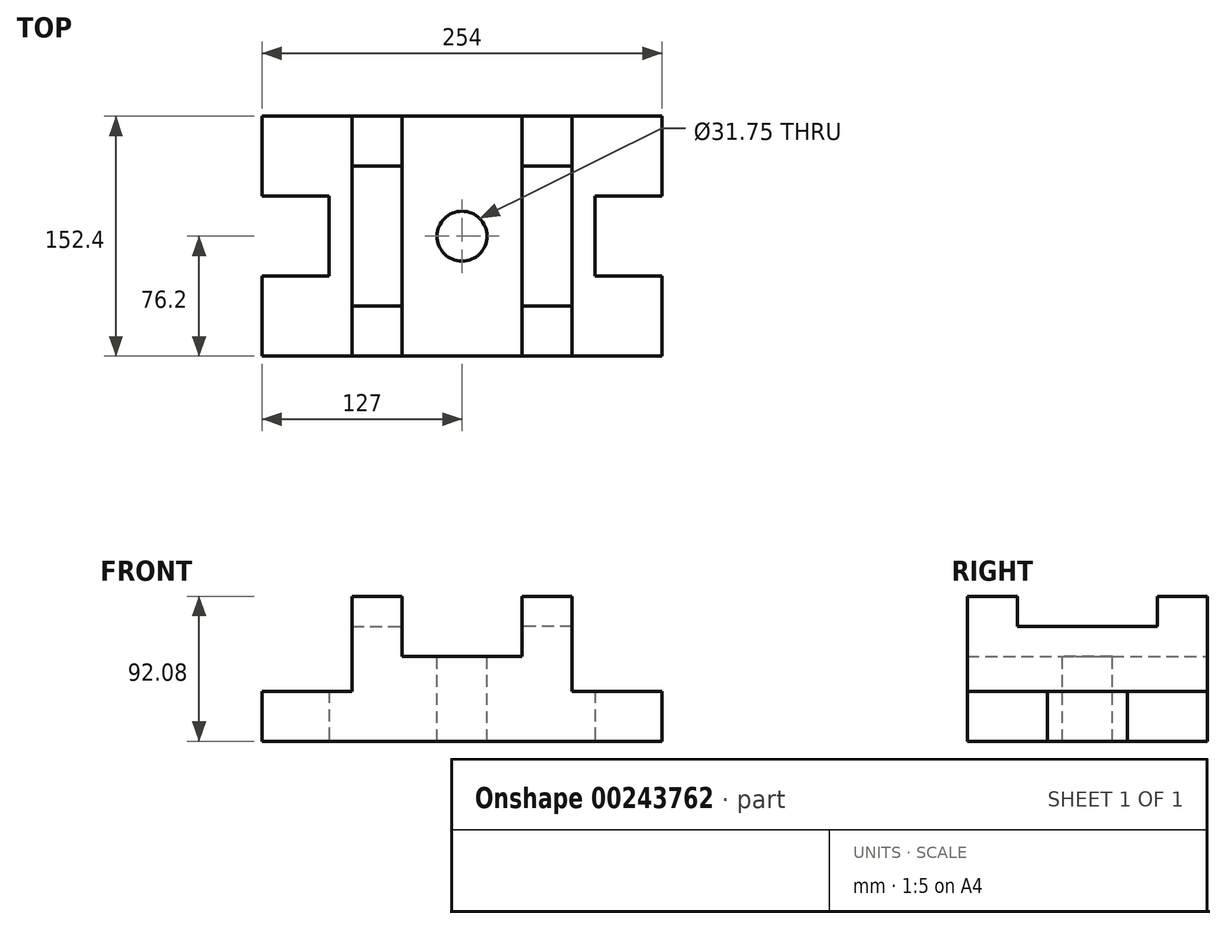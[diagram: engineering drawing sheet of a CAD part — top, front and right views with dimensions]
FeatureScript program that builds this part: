
annotation { "Feature Type Name" : "Feature", "Feature Type Description" : "" }
export const myFeature = defineFeature(function(context is Context, id is Id, definition is map)
    precondition{}
    {
        {
            var Q0;
            Q0=qCreatedBy(makeId("Front.planeOp"),FACE);
            var sketch = newSketch(context, id + "F0", { "sketchPlane" : qUnion([Q0])});
            skLineSegment(sketch, "E0", {"start": v(0, 0) * mm, "end": v(-63.5, 0) * mm});
            skLineSegment(sketch, "E1", {"start": v(0, 0) * mm, "end": v(63.5, 0) * mm});
            skLineSegment(sketch, "E2", {"start": v(63.5, 0) * mm, "end": v(63.5, 31.75) * mm});
            skLineSegment(sketch, "E3", {"start": v(63.5, 31.75) * mm, "end": v(6.35, 31.75) * mm});
            skLineSegment(sketch, "E4", {"start": v(6.35, 31.75) * mm, "end": v(6.35, 92.07) * mm});
            skLineSegment(sketch, "E5", {"start": v(6.35, 92.07) * mm, "end": v(-25.4, 92.07) * mm});
            skLineSegment(sketch, "E6", {"start": v(-25.4, 92.07) * mm, "end": v(-25.4, 53.97) * mm});
            skLineSegment(sketch, "E7", {"start": v(-25.4, 53.97) * mm, "end": v(-63.5, 53.97) * mm});
            skLineSegment(sketch, "E8", {"start": v(-63.5, 0) * mm, "end": v(-63.5, 53.97) * mm});
            skSolve(sketch);
        }
        {
            var Q0;
            Q0=makeQuery(id+"F0.imprint","IMPRINT",FACE,{"disambiguationData":[TD([[makeQuery(id+"F0.imprint","IMPRINT",EDGE,{"derivedFrom":sQuery(id+"F0.wireOp",EDGE,"E8")}),1.0]])]});
            var Q1;
            Q1=makeQuery(id+"F0.imprint","IMPRINT",FACE,{"disambiguationData":[TD([[makeQuery(id+"F0.imprint","IMPRINT",EDGE,{"derivedFrom":sQuery(id+"F0.wireOp",EDGE,"E0")}),-1.0]])]});
            extrude(context, id + "F1", {"entities" : qUnion([Q0, Q1]), "depth" : 152.4 * mm});
        }
        {
            var Q0;
            Q0=makeQuery(id+"F1.opExtrude","SWEPT_FACE",FACE,{"disambiguationData":[OSD([sQuery(id+"F0.wireOp",EDGE,"E2")])]});
            var sketch = newSketch(context, id + "F2", { "sketchPlane" : qUnion([Q0])});
            skPoint(sketch, "E9", {"position": v(-101.6, 31.75) * mm});
            skLineSegment(sketch, "E10", {"start": v(-101.6, 31.75) * mm, "end": v(-101.6, 0) * mm});
            skPoint(sketch, "E11", {"position": v(-50.8, 31.75) * mm});
            skLineSegment(sketch, "E12", {"start": v(-50.8, 31.75) * mm, "end": v(-50.8, 0) * mm});
            skSolve(sketch);
        }
        {
            var Q0;
            {var subQ0=sQuery(id+"F2.wireOp",EDGE,"E10");Q0=makeQuery(id+"F2.imprint","IMPRINT",FACE,{"disambiguationData":[TD([[makeQuery(id+"F2.imprint","IMPRINT",EDGE,{"derivedFrom":subQ0}),1.0]])]});}
            extrude(context, id + "F3", {"entities" : qUnion([Q0]), "operationType" : NewBodyOperationType.REMOVE, "oppositeDirection" : true, "depth" : 42.55 * mm});
        }
        {
            var Q0;
            Q0=makeQuery(id+"F1.opExtrude","SWEPT_FACE",FACE,{"disambiguationData":[OSD([sQuery(id+"F0.wireOp",EDGE,"E5")])]});
            var sketch = newSketch(context, id + "F4", { "sketchPlane" : qUnion([Q0])});
            skPoint(sketch, "E13", {"position": v(6.35, -120.65) * mm});
            skLineSegment(sketch, "E14", {"start": v(6.35, -120.65) * mm, "end": v(-25.4, -120.65) * mm});
            skPoint(sketch, "E15", {"position": v(6.35, -31.75) * mm});
            skLineSegment(sketch, "E16", {"start": v(6.35, -31.75) * mm, "end": v(-25.4, -31.75) * mm});
            skSolve(sketch);
        }
        {
            var Q0;
            {var subQ0=sQuery(id+"F4.wireOp",EDGE,"E14");Q0=makeQuery(id+"F4.imprint","IMPRINT",FACE,{"disambiguationData":[TD([[makeQuery(id+"F4.imprint","IMPRINT",EDGE,{"derivedFrom":subQ0}),-1.0]])]});}
            extrude(context, id + "F5", {"entities" : qUnion([Q0]), "operationType" : NewBodyOperationType.REMOVE, "oppositeDirection" : true, "depth" : 19.05 * mm});
        }
        {
            var Q0;
            Q0=makeQuery(id+"F1.opExtrude","SWEPT_BODY",BODY,{"disambiguationData":[OSD([sQuery(id+"F0.wireOp",EDGE,"E0"),sQuery(id+"F0.wireOp",EDGE,"E1"),sQuery(id+"F0.wireOp",EDGE,"E2"),sQuery(id+"F0.wireOp",EDGE,"E3"),sQuery(id+"F0.wireOp",EDGE,"E4"),sQuery(id+"F0.wireOp",EDGE,"E5"),sQuery(id+"F0.wireOp",EDGE,"E6"),sQuery(id+"F0.wireOp",EDGE,"E7"),sQuery(id+"F0.wireOp",EDGE,"E8")])]});
            var Q1;
            Q1=makeQuery(id+"F1.opExtrude","SWEPT_FACE",FACE,{"disambiguationData":[OSD([sQuery(id+"F0.wireOp",EDGE,"E8")])]});
            mirror(context, id + "F6", {"operationType" : NewBodyOperationType.ADD, "entities" : qUnion([Q0]), "mirrorPlane" : qUnion([Q1])});
        }
        {
            var Q0;
            {var subQ0=makeQuery(id+"F1.opExtrude","SWEPT_FACE",FACE,{"disambiguationData":[OSD([sQuery(id+"F0.wireOp",EDGE,"E7")])]});Q0=makeQuery(id+"F6.boolean.opBoolean","MERGE",FACE,{"derivedFrom":[subQ0,makeQuery(id+"F6.opPattern","COPY",FACE,{"derivedFrom":subQ0,"instanceName":"1"})]});}
            var sketch = newSketch(context, id + "F7", { "sketchPlane" : qUnion([Q0])});
            skPoint(sketch, "E17", {"position": v(-63.5, -152.4) * mm});
            skPoint(sketch, "E18", {"position": v(-63.5, -76.2) * mm});
            skCircle(sketch, "E19", {"center": v(-63.5, -76.2) * mm, "radius": 15.88 * mm});
            skSolve(sketch);
        }
        {
            var Q0;
            Q0=makeQuery(id+"F7.imprint","IMPRINT",FACE,{"disambiguationData":[TD([[makeQuery(id+"F7.imprint","IMPRINT",EDGE,{"derivedFrom":sQuery(id+"F7.wireOp",EDGE,"E19")}),1.0]])]});
            extrude(context, id + "F8", {"entities" : qUnion([Q0]), "operationType" : NewBodyOperationType.REMOVE, "oppositeDirection" : true, "depth" : 55.88 * mm});
        }
    });
